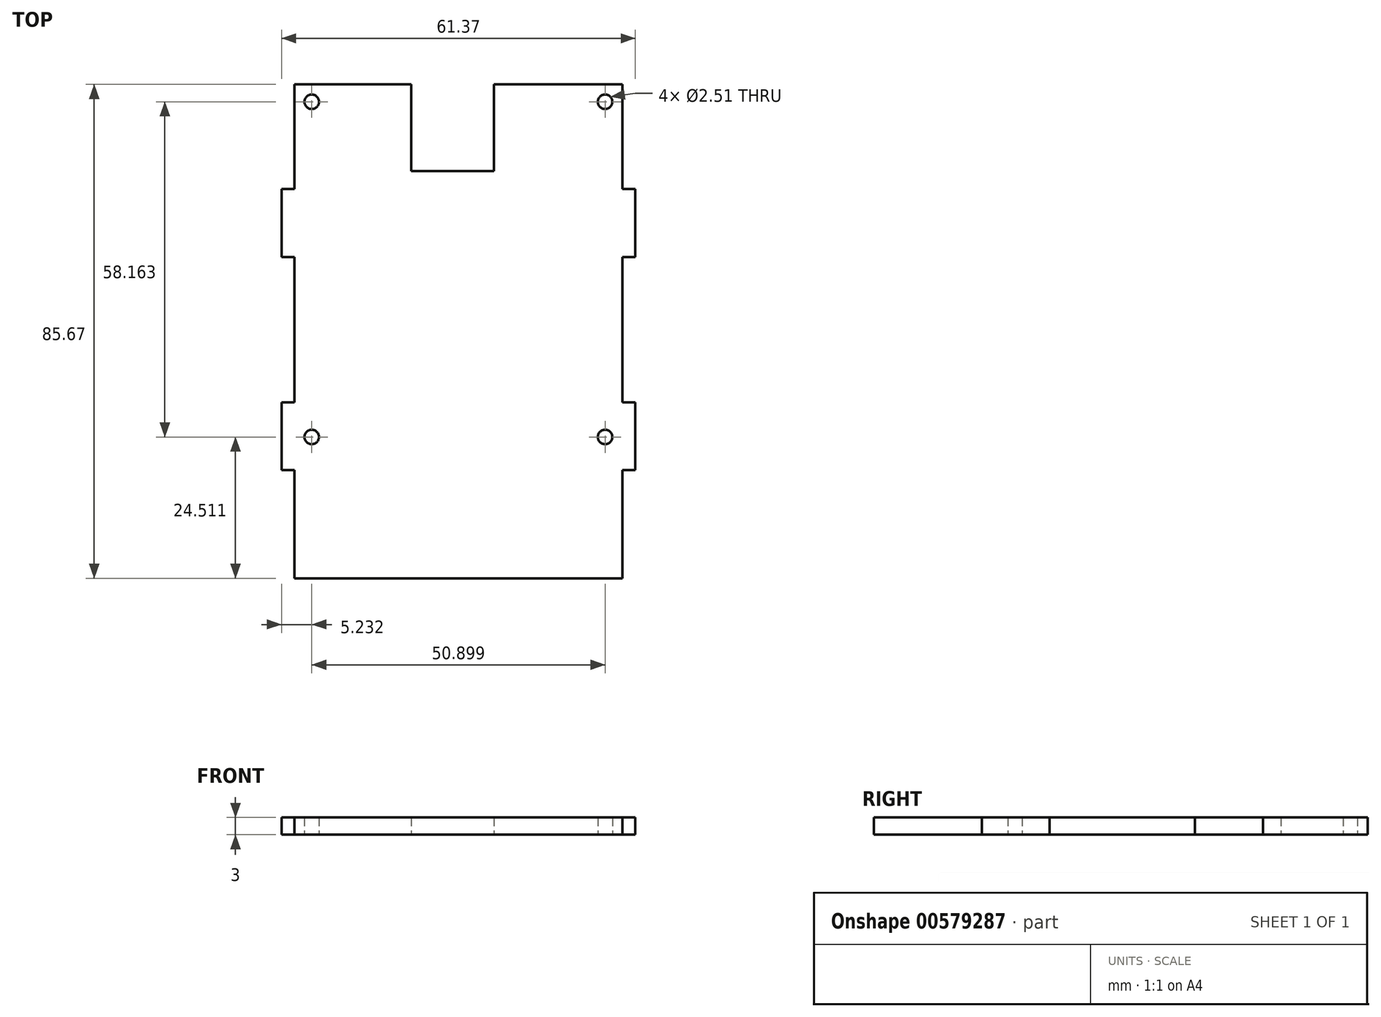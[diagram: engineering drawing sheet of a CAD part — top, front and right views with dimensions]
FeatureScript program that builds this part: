
annotation { "Feature Type Name" : "Feature", "Feature Type Description" : "" }
export const myFeature = defineFeature(function(context is Context, id is Id, definition is map)
    precondition{}
    {
        {
            var Q0;
            Q0=qCreatedBy(makeId("Top.planeOp"),FACE);
            var sketch = newSketch(context, id + "F0", { "sketchPlane" : qUnion([Q0])});
            skLineSegment(sketch, "E0.bottom", {"start": v(-25.1, -42.68) * mm, "end": v(-4.84, -42.68) * mm});
            skLineSegment(sketch, "E0.top", {"start": v(-25.1, -128.35) * mm, "end": v(31.8, -128.35) * mm});
            skLineSegment(sketch, "E0.left", {"start": v(-25.1, -42.68) * mm, "end": v(-25.1, -60.84) * mm});
            skLineSegment(sketch, "E0.right", {"start": v(31.8, -42.68) * mm, "end": v(31.8, -60.84) * mm});
            skLineSegment(sketch, "E1.top", {"start": v(-4.84, -57.69) * mm, "end": v(9.49, -57.69) * mm});
            skLineSegment(sketch, "E1.left", {"start": v(-4.84, -42.68) * mm, "end": v(-4.84, -57.69) * mm});
            skLineSegment(sketch, "E1.right", {"start": v(9.49, -42.68) * mm, "end": v(9.49, -57.69) * mm});
            skLineSegment(sketch, "E2.bottom", {"start": v(31.8, -60.84) * mm, "end": v(34.03, -60.84) * mm});
            skLineSegment(sketch, "E2.top", {"start": v(31.8, -72.62) * mm, "end": v(34.03, -72.62) * mm});
            skLineSegment(sketch, "E2.right", {"start": v(34.03, -60.84) * mm, "end": v(34.03, -72.62) * mm});
            skLineSegment(sketch, "E3.bottom", {"start": v(31.8, -97.82) * mm, "end": v(34.03, -97.82) * mm});
            skLineSegment(sketch, "E3.top", {"start": v(31.8, -109.6) * mm, "end": v(34.03, -109.6) * mm});
            skLineSegment(sketch, "E3.right", {"start": v(34.03, -97.82) * mm, "end": v(34.03, -109.6) * mm});
            skCircle(sketch, "E4", {"center": v(28.8, -103.84) * mm, "radius": 1.26 * mm});
            skCircle(sketch, "E5", {"center": v(28.8, -45.68) * mm, "radius": 1.26 * mm});
            skPoint(sketch, "E6.orphan", {"position": v(27.09, -42.68) * mm});
            skLineSegment(sketch, "E7.trimOffspring", {"start": v(31.8, -72.62) * mm, "end": v(31.8, -97.82) * mm});
            skLineSegment(sketch, "E8.trimOffspring", {"start": v(31.8, -109.6) * mm, "end": v(31.8, -128.35) * mm});
            skLineSegment(sketch, "E9.MirrorCS", {"start": v(-25.1, -97.82) * mm, "end": v(-27.34, -97.82) * mm});
            skLineSegment(sketch, "E10.MirrorCS", {"start": v(-25.1, -109.6) * mm, "end": v(-27.34, -109.6) * mm});
            skLineSegment(sketch, "E11.MirrorCS", {"start": v(-25.1, -72.62) * mm, "end": v(-27.34, -72.62) * mm});
            skLineSegment(sketch, "E12.MirrorCS", {"start": v(-25.1, -60.84) * mm, "end": v(-27.34, -60.84) * mm});
            skLineSegment(sketch, "E13.MirrorCS", {"start": v(-27.34, -97.82) * mm, "end": v(-27.34, -109.6) * mm});
            skLineSegment(sketch, "E14.MirrorCS", {"start": v(-27.34, -60.84) * mm, "end": v(-27.34, -72.62) * mm});
            skLineSegment(sketch, "E15.MirrorCS", {"start": v(-25.1, -72.62) * mm, "end": v(-25.1, -97.82) * mm});
            skLineSegment(sketch, "E16.MirrorCS", {"start": v(-25.1, -109.6) * mm, "end": v(-25.1, -128.35) * mm});
            skPoint(sketch, "E17.MirrorP", {"position": v(-20.4, -42.68) * mm});
            skCircle(sketch, "E18.MirrorC", {"center": v(-22.1, -103.84) * mm, "radius": 1.26 * mm});
            skCircle(sketch, "E19.MirrorC", {"center": v(-22.1, -45.68) * mm, "radius": 1.26 * mm});
            skPoint(sketch, "E20.start.orphan", {"position": v(3.34, -128.35) * mm});
            skLineSegment(sketch, "E21.trimOffspring", {"start": v(9.49, -42.68) * mm, "end": v(31.8, -42.68) * mm});
            skSolve(sketch);
        }
        {
            var Q0;
            Q0 = qSketchRegion(id + "F0", true);
            extrude(context, id + "F1", {"entities" : qUnion([Q0]), "depth" : 3 * mm, "offsetDistance" : 25.4 * mm});
        }
    });
